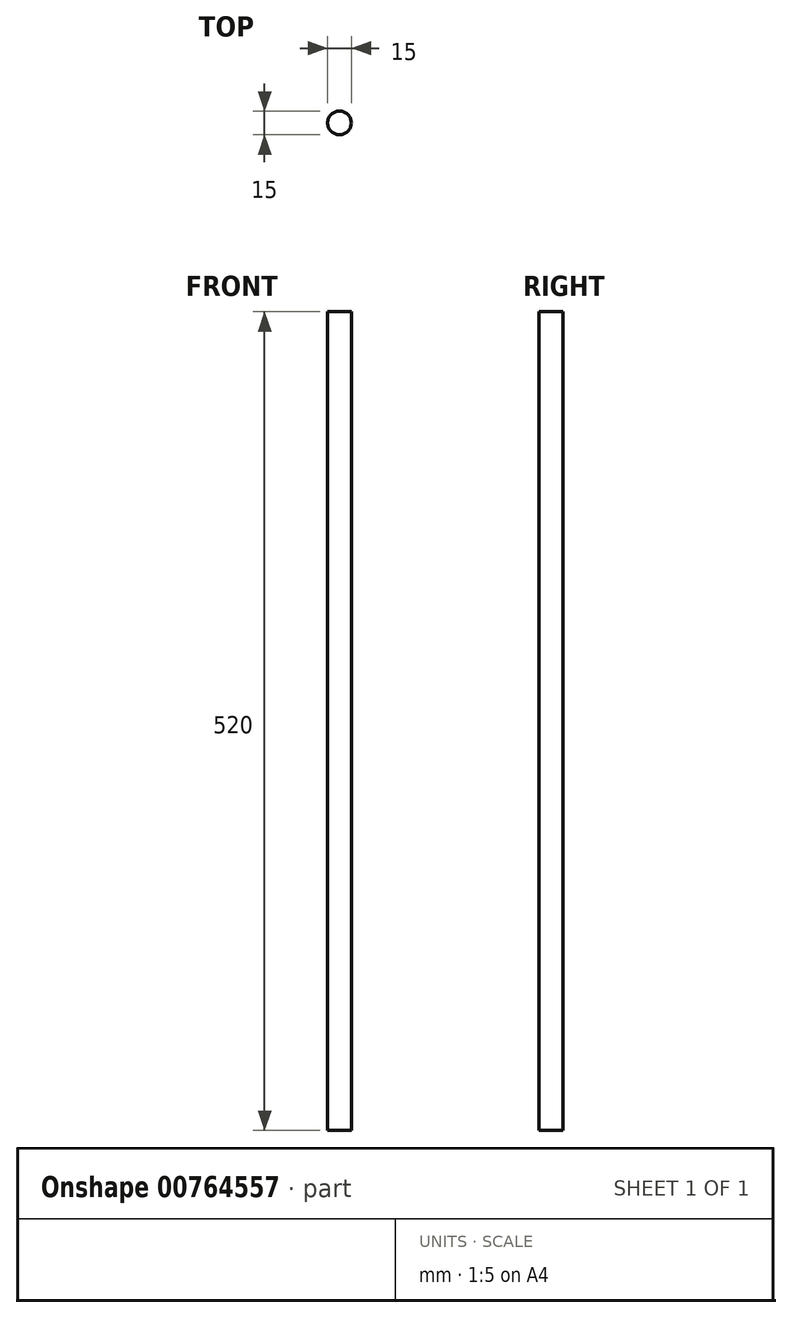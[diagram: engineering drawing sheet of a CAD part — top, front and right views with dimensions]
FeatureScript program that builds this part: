
annotation { "Feature Type Name" : "Feature", "Feature Type Description" : "" }
export const myFeature = defineFeature(function(context is Context, id is Id, definition is map)
    precondition{}
    {
        {
            var Q0;
            Q0=qCreatedBy(makeId("Top.planeOp"),FACE);
            var sketch = newSketch(context, id + "F0", { "sketchPlane" : qUnion([Q0])});
            skCircle(sketch, "E0", {"center": v(0, 0.48) * mm, "radius": 7.5 * mm});
            skSolve(sketch);
        }
        {
            var Q0;
            Q0 = qSketchRegion(id + "F0", true);
            extrude(context, id + "F1", {"entities" : qUnion([Q0]), "depth" : 520 * mm, "offsetDistance" : 25 * mm});
        }
    });
